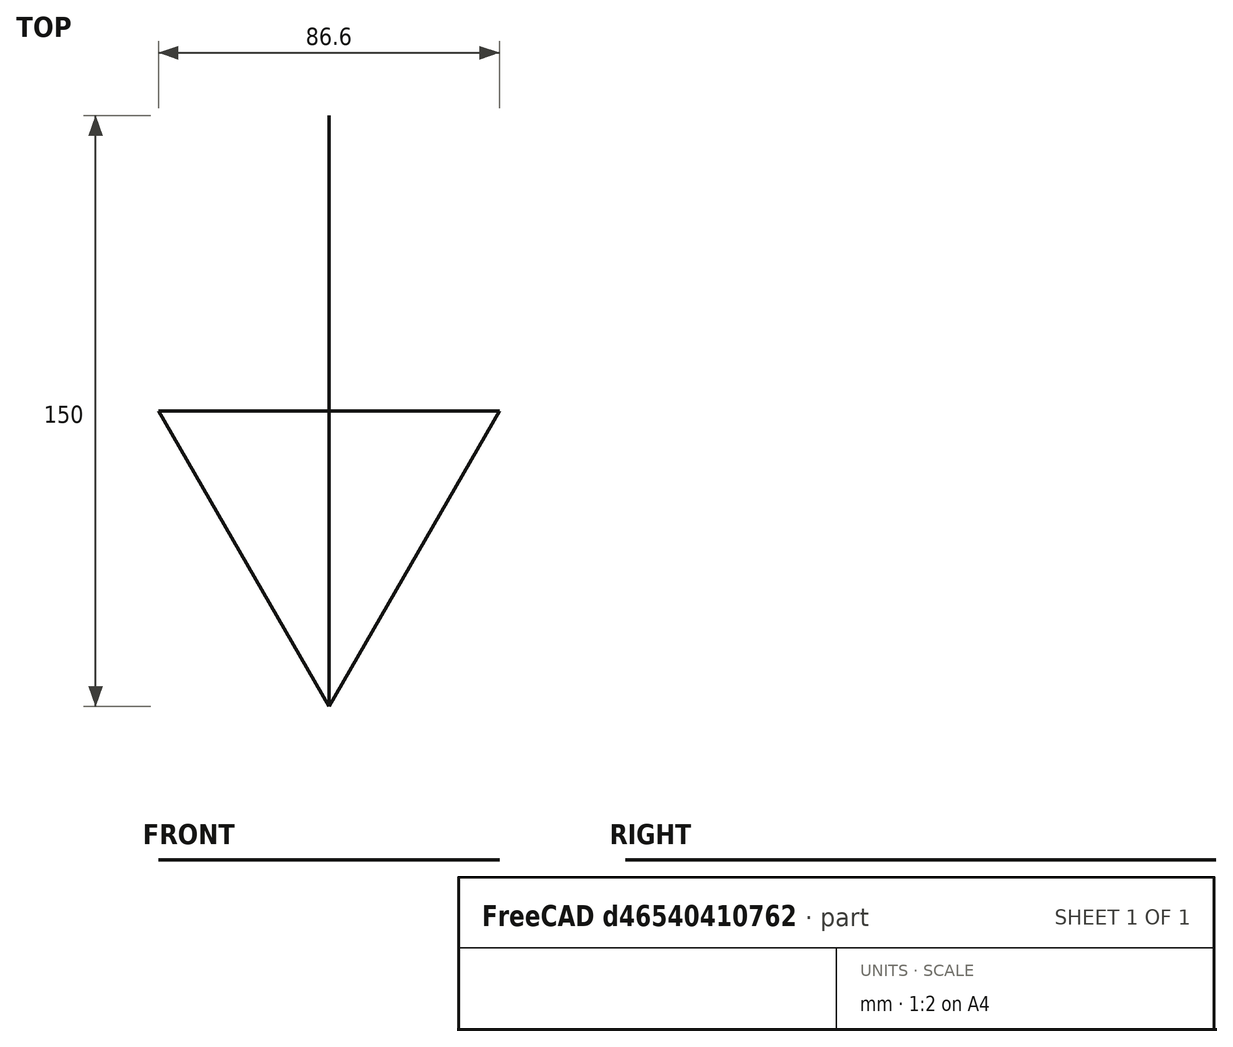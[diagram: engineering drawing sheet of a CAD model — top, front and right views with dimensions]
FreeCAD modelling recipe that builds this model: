
FCSTD DOCUMENT  (FreeCAD 1.1R20260325 (Git shallow))
Label: Tomada_Media_1modulo_220v_com_simbologia
License: All rights reserved
LicenseURL: http://en.wikipedia.org/wiki/All_rights_reserved
objects: Part::FeaturePython×1, Part::Feature×1, App::DocumentObjectGroup×1
note: 2 computed .brp shape members not serialized (recipe doc carries the construction recipe); baked Part::Feature solids carry a one-line shape summary decoded from their .brp

FEATURE [Part::FeaturePython] Component  label="Tomada_1modulo_220v"  # Arch/BIM 0 (typed FeaturePython)
  HorizontalArea = 0
  IfcData = attributes={"GlobalId": {"name": "GlobalId", "type": "IfcGloballyUniqueId", "is_enum": false, "enum_values": []}, "Description": {"... (+538 chars omitted),+1 more (map truncated)
  IfcType = 0
  MoveBase = false
  MoveWithHost = false
  PerimeterLength = 0
  Placement = pos=(0,0,1200) rot=(0,0,1;0rad)
  PredefinedType = 0
  VerticalArea = 0
FEATURE [Part::Feature] Compound002002002004005002002003003002003005002002005002002002002002002002002002002001  label="Simbologia_Tomada_Media"
  Placement = pos=(871.053,2055.85,1190.37) rot=(0,0,-1;1.5708rad)
  shape: bbox 86.6 x 150 x 2e-07 mm, 1 faces, 0 solids (baked)
FEATURE [App::DocumentObjectGroup] Group  label="Tomada_1modulo_Media"
  Group = -> [Component,Compound002002002004005002002003003002003005002002005002002002002002002002002002002001]
